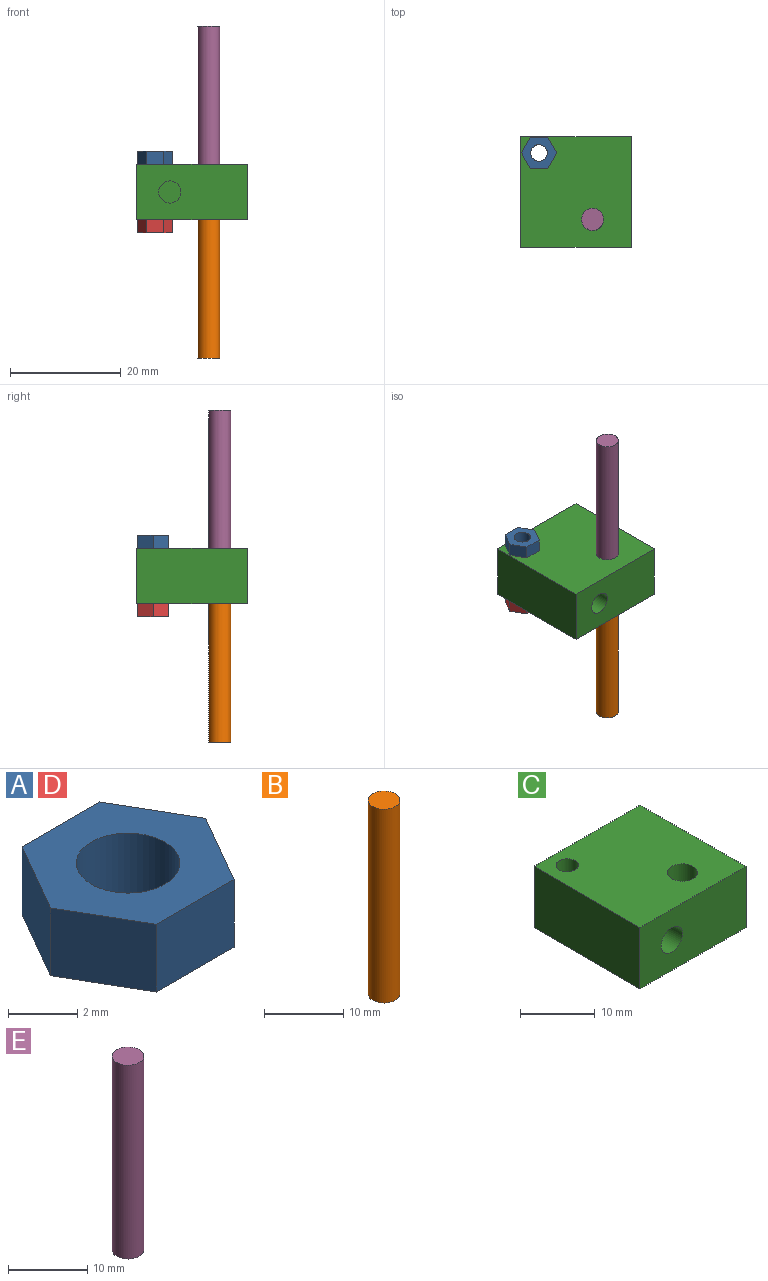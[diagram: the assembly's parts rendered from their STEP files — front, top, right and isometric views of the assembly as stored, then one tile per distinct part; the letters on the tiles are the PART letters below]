
ASSEMBLY  parts=5 mates=4
PART A: 9 faces, bbox 6.4x5.5x2.4 mm
  f0: plane 2.75x2.4mm, normal (-0.87,-0.5,0), area 7.6mm2, adj f1,f5,f7,f8
  f1: plane 2.75x2.4mm, normal (-0.87,0.5,0), area 7.6mm2, adj f0,f2,f7,f8
  f2: plane 3.18x2.4mm, normal (0,1,0), area 7.6mm2, adj f1,f3,f7,f8
  f3: plane 2.75x2.4mm, normal (0.87,0.5,0), area 7.6mm2, adj f2,f4,f7,f8
  f4: plane 2.75x2.4mm, normal (0.87,-0.5,0), area 7.6mm2, adj f3,f5,f7,f8
  f5: plane 3.18x2.4mm, normal (0,-1,0), area 7.6mm2, adj f0,f4,f7,f8
  f6: cylinder r=1.5mm len=3mm, axis (0,0,1), area 22.6mm2, adj f7,f8
  f7: plane 6.35x5.5mm, normal (0,0,-1), area 19.1mm2, adj f0,f1,f2,f3,f4,f5,f6
  f8: plane 6.35x5.5mm, normal (0,0,1), area 19.1mm2, adj f0,f1,f2,f3,f4,f5,f6
PART B: 3 faces, bbox 4x4x30 mm
  f0: cylinder r=2mm len=30mm, axis (0,0,1), area 377mm2, adj f1,f2
  f1: plane 4x4mm, normal (0,0,-1), area 12.6mm2, adj f0
  f2: plane 4x4mm, normal (0,0,1), area 12.6mm2, adj f0
PART C: 12 faces, bbox 20x20x10 mm
  f0: plane 20x10mm, normal (1,0,0), area 171.7mm2, adj f1,f3,f6,f7,f10
  f1: plane 20x10mm, normal (0,-1,0), area 187.4mm2, adj f0,f2,f6,f7,f8
  f2: plane 20x10mm, normal (-1,0,0), area 200mm2, adj f1,f3,f6,f7
  f3: plane 20x10mm, normal (0,1,0), area 200mm2, adj f0,f2,f6,f7
  f4: cylinder r=1.5mm len=10mm, axis (0,0,1), area 94.2mm2, adj f6,f7
  f5: cylinder r=2mm len=10mm, axis (0,0,1), area 125.7mm2, adj f6,f7
  f6: plane 20x20mm, normal (0,0,-1), area 380.4mm2, adj f0,f1,f2,f3,f4,f5
  f7: plane 20x20mm, normal (0,0,1), area 380.4mm2, adj f0,f1,f2,f3,f4,f5
  f8: cylinder r=2mm len=10mm, axis (0,-1,0), area 125.7mm2, adj f1,f9
  f9: plane 4x4mm, normal (0,-1,0), area 12.6mm2, adj f8
  f10: cylinder r=3mm len=10mm, axis (1,0,0), area 188.5mm2, adj f0,f11
  f11: plane 6x6mm, normal (1,0,0), area 28.3mm2, adj f10
PART D: same geometry as A
PART E: 3 faces, bbox 4x4x30 mm
  f0: cylinder r=2mm len=30mm, axis (0,0,-1), area 377mm2, adj f1,f2
  f1: plane 4x4mm, normal (0,0,1), area 12.6mm2, adj f0
  f2: plane 4x4mm, normal (0,0,-1), area 12.6mm2, adj f0
PLACE A t=(5.76,-55.31,-40.33)mm
PLACE B t=(5.76,-55.31,-42.73)mm
PLACE C t=(5.76,-55.31,-42.73)mm
PLACE D t=(5.76,-55.31,-52.73)mm
PLACE E t=(5.76,-55.31,-42.73)mm
MATE fastened A.f6 <-> C.f4  axis (0,0,1) through (-0.92,-48.26,-82.73)mm
MATE fastened E.f0 <-> C.f5  axis (0,0,-1) through (8.76,-60.31,-87.73)mm
MATE fastened D.f6 <-> C.f4  axis (0,0,1) through (-0.92,-48.26,-92.73)mm
MATE fastened B.f0 <-> E.f0  axis (0,0,1) through (8.76,-60.31,-87.73)mm
